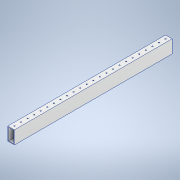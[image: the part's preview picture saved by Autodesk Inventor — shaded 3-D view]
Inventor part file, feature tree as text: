
AUTODESK INVENTOR PART (.ipt)
format: ipt  version: 2020 (Build 240168000, 168)  size: 154,624 bytes
history: native  units: in
note: dims shown in document units (in); Inventor stores cm internally (conversion verified against a paired STEP export)
features: sketch x2, extrude x1, hole x1
ambient origin geometry x8: Origin, YZ Plane, XZ Plane, XY Plane, X Axis, Y Axis, Z Axis, Center Point
bodies: Solid1 (feature_tree)
feature tree (4):
  extrude  "Extrusion1"  Depth=2.0in
  hole  "Hole1"  [1 undecoded]
  sketch  "Sketch1"  dims[d0=1.0in d1=2.0in]
  sketch  "Sketch2"  dims[d2=0.1in d3=24.0in d4=0.0in d5=0.5in d6=0.5in d7=9.4488in d9=1.0in d10=0.3937in d12=1.0in d14=0.163in d15=0.75in d16=0.375in d17=0.25in d18=0.5635in d19=1.0in d20=0.8108in]
note: 1 required parameter value undecoded (feature->parameter linkage not recoverable at this tier; creation-order binding heuristic only, values carry confidence <= 0.55)
